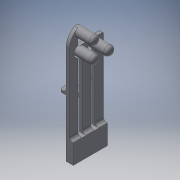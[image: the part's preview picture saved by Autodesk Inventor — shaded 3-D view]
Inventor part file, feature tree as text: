
AUTODESK INVENTOR PART (.ipt)
format: ipt  version: 2016 (Build 200138000, 138)  size: 300,032 bytes
history: native  units: in
note: dims shown in document units (in); Inventor stores cm internally (conversion verified against a paired STEP export)
features: reference x8, projected_geometry x6, extrude x5, sketch x5, fillet x4, plane x3
ambient origin geometry x8: Origin, YZ Plane, XZ Plane, XY Plane, X Axis, Y Axis, Z Axis, Center Point
bodies: Solid1 (feature_tree)
feature tree (31):
  extrude  "Extrusion1"  Depth=0.0079in
  sketch  "Sketch2"  dims[d11=0.0079in d12=0.052in d13=0.052in]
  plane  "Work Plane1"
  plane  "Work Plane2"
  extrude  "Extrusion2"  Depth=0.052in
  fillet  "Fillet1"  Radius=0.052in
  extrude  "Extrusion3"  Depth=0.0079in
  sketch  "Sketch4"  dims[d16=0.025in d17=0.025in d18=0.0197in d19=0.0in]
  plane  "Work Plane3"
  extrude  "Extrusion4"  Depth=0.0197in
  fillet  "Fillet2"  Radius=0.0197in
  extrude  "Extrusion5"  Depth=0.0197in
  fillet  "Fillet3"  Radius=0.1969in
  fillet  "Fillet4"  Radius=0.1181in
  sketch  "Sketch1"  dims[d9=0.0079in d10=0.0079in]
  reference  "Reference1"
  reference  "Reference2"
  reference  "Reference3"
  reference  "Reference4"
  reference  "Reference5"
  sketch  "Sketch3"  dims[d14=0.052in d15=0.0079in]
  projected_geometry  "Projected Loop1"
  projected_geometry  "Projected Loop2"
  projected_geometry  "Projected Loop3"
  projected_geometry  "Projected Loop4"
  projected_geometry  "Projected Loop5"
  projected_geometry  "Projected Loop6"
  sketch  "Sketch5"  dims[d20=0.0197in d21=0.0in d22=0.0197in d23=0.1969in d24=0.0in d25=0.1181in d26=0.1969in d27=0.0in d28=0.0197in d29=0.0394in d30=0.0394in d31=0.1181in d32=0.0394in d33=0.0in d34=0.0157in d35=0.0157in]
  reference  "Reference6"
  reference  "Reference7"
  reference  "Reference8"
